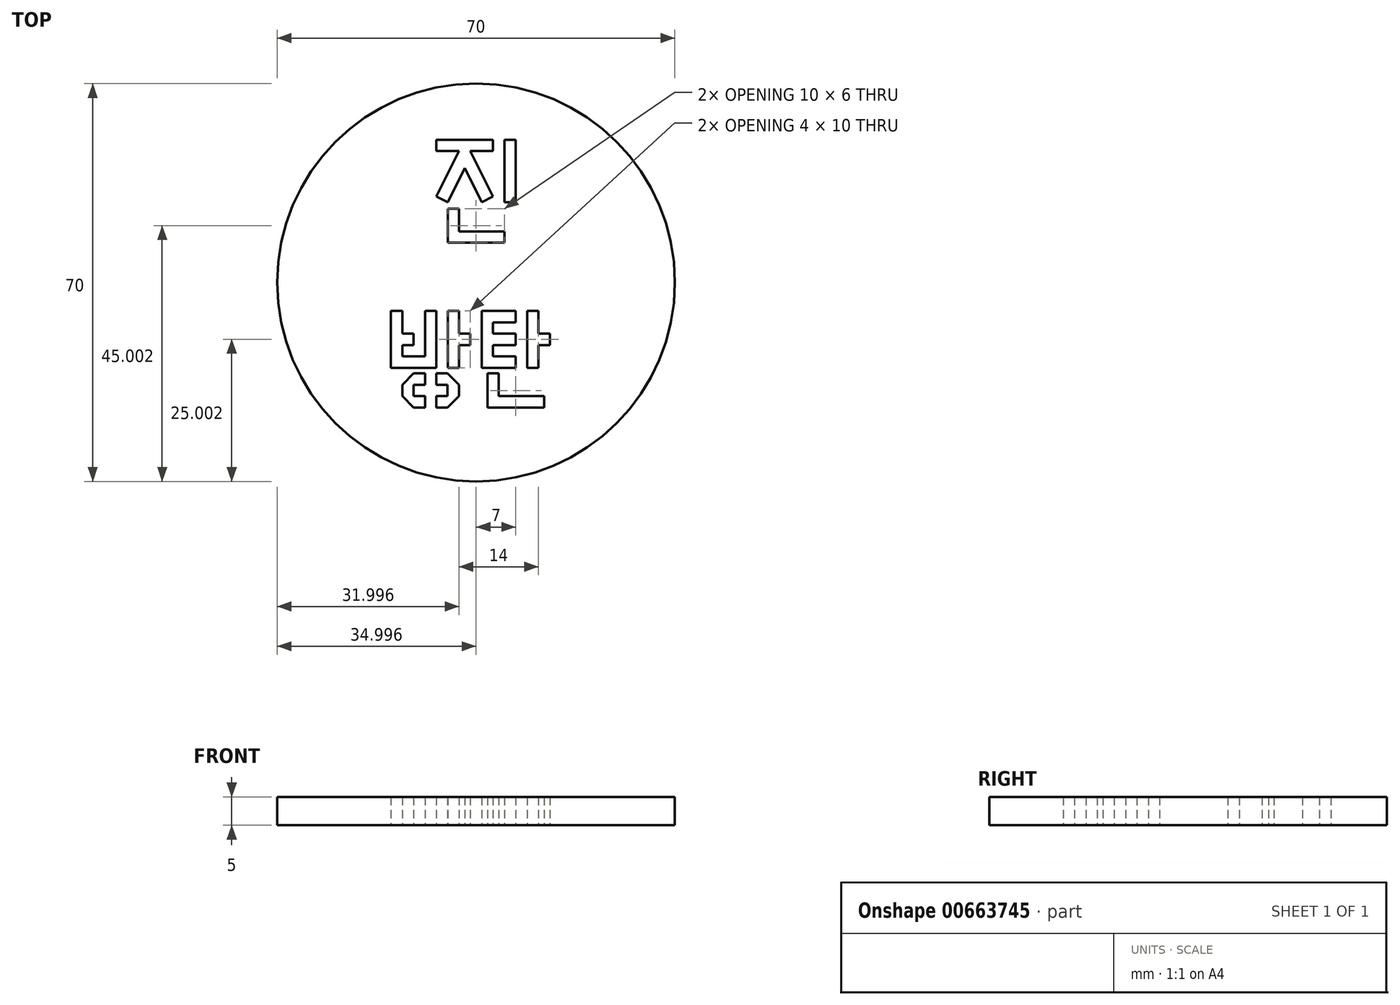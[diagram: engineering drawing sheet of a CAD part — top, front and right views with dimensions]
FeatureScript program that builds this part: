
annotation { "Feature Type Name" : "Feature", "Feature Type Description" : "" }
export const myFeature = defineFeature(function(context is Context, id is Id, definition is map)
    precondition{}
    {
        {
            var Q0;
            Q0=qCreatedBy(makeId("Top.planeOp"),FACE);
            var sketch = newSketch(context, id + "F0", { "sketchPlane" : qUnion([Q0])});
            skLineSegment(sketch, "E0.bottom", {"start": v(-33.94, 20.88) * mm, "end": v(-23.94, 20.88) * mm});
            skLineSegment(sketch, "E0.left", {"start": v(-33.94, 20.88) * mm, "end": v(-33.94, 18.88) * mm});
            skLineSegment(sketch, "E0.right", {"start": v(-23.94, 20.88) * mm, "end": v(-23.94, 18.88) * mm});
            skLineSegment(sketch, "E1", {"start": v(-33.94, 18.88) * mm, "end": v(-29.94, 18.88) * mm});
            skLineSegment(sketch, "E2", {"start": v(-29.94, 18.88) * mm, "end": v(-33.94, 10.88) * mm});
            skLineSegment(sketch, "E3", {"start": v(-33.94, 10.88) * mm, "end": v(-31.94, 9.88) * mm});
            skLineSegment(sketch, "E4", {"start": v(-31.94, 9.88) * mm, "end": v(-28.94, 15.88) * mm});
            skLineSegment(sketch, "E5", {"start": v(-28.94, 15.88) * mm, "end": v(-25.94, 9.88) * mm});
            skLineSegment(sketch, "E6", {"start": v(-25.94, 9.88) * mm, "end": v(-23.94, 10.88) * mm});
            skLineSegment(sketch, "E7", {"start": v(-27.94, 18.88) * mm, "end": v(-23.94, 10.88) * mm});
            skLineSegment(sketch, "E8.bottom", {"start": v(-21.94, 9.88) * mm, "end": v(-19.94, 9.88) * mm});
            skLineSegment(sketch, "E8.left", {"start": v(-21.94, 9.88) * mm, "end": v(-21.94, 20.88) * mm});
            skLineSegment(sketch, "E9", {"start": v(-29.94, 5.75) * mm, "end": v(-29.94, 8.75) * mm});
            skLineSegment(sketch, "E10.bottom", {"start": v(-25.94, -9.25) * mm, "end": v(-19.94, -9.25) * mm});
            skLineSegment(sketch, "E10.top", {"start": v(-25.94, -19.25) * mm, "end": v(-19.94, -19.25) * mm});
            skLineSegment(sketch, "E10.left", {"start": v(-25.94, -9.25) * mm, "end": v(-25.94, -19.25) * mm});
            skLineSegment(sketch, "E10.right", {"start": v(-19.94, -9.25) * mm, "end": v(-19.94, -11.25) * mm});
            skLineSegment(sketch, "E11", {"start": v(-19.94, -11.25) * mm, "end": v(-23.94, -11.25) * mm});
            skLineSegment(sketch, "E12", {"start": v(-23.94, -11.25) * mm, "end": v(-23.94, -13.25) * mm});
            skLineSegment(sketch, "E13", {"start": v(-23.94, -13.25) * mm, "end": v(-19.94, -13.25) * mm});
            skLineSegment(sketch, "E14", {"start": v(-19.94, -13.25) * mm, "end": v(-19.94, -15.25) * mm});
            skLineSegment(sketch, "E15", {"start": v(-19.94, -15.25) * mm, "end": v(-23.94, -15.25) * mm});
            skLineSegment(sketch, "E16", {"start": v(-23.94, -15.25) * mm, "end": v(-23.94, -17.25) * mm});
            skLineSegment(sketch, "E17", {"start": v(-23.94, -17.25) * mm, "end": v(-19.94, -17.25) * mm});
            skLineSegment(sketch, "E18.bottom", {"start": v(-17.94, -9.25) * mm, "end": v(-15.94, -9.25) * mm});
            skLineSegment(sketch, "E18.top", {"start": v(-17.94, -19.25) * mm, "end": v(-15.94, -19.25) * mm});
            skLineSegment(sketch, "E18.left", {"start": v(-17.94, -9.25) * mm, "end": v(-17.94, -19.25) * mm});
            skLineSegment(sketch, "E18.right", {"start": v(-15.94, -9.25) * mm, "end": v(-15.94, -13.25) * mm});
            skLineSegment(sketch, "E19.bottom", {"start": v(-15.94, -13.25) * mm, "end": v(-13.94, -13.25) * mm});
            skLineSegment(sketch, "E19.top", {"start": v(-15.94, -15.25) * mm, "end": v(-13.94, -15.25) * mm});
            skLineSegment(sketch, "E19.right", {"start": v(-13.94, -13.25) * mm, "end": v(-13.94, -15.25) * mm});
            skLineSegment(sketch, "E20", {"start": v(-25.94, -19.25) * mm, "end": v(-24.94, -19.25) * mm});
            skLineSegment(sketch, "E21", {"start": v(-24.94, -20.25) * mm, "end": v(-24.94, -26.25) * mm});
            skLineSegment(sketch, "E22", {"start": v(-24.94, -26.25) * mm, "end": v(-14.94, -26.25) * mm});
            skLineSegment(sketch, "E23", {"start": v(-14.94, -26.25) * mm, "end": v(-14.94, -24.25) * mm});
            skLineSegment(sketch, "E24", {"start": v(-14.94, -24.25) * mm, "end": v(-22.94, -24.25) * mm});
            skLineSegment(sketch, "E25", {"start": v(-22.94, -24.25) * mm, "end": v(-22.94, -20.25) * mm});
            skLineSegment(sketch, "E26", {"start": v(-22.94, -20.25) * mm, "end": v(-24.94, -20.25) * mm});
            skLineSegment(sketch, "E27", {"start": v(-29.94, -9.25) * mm, "end": v(-31.94, -9.25) * mm});
            skLineSegment(sketch, "E28", {"start": v(-41.94, -9.25) * mm, "end": v(-41.94, -19.25) * mm});
            skLineSegment(sketch, "E29", {"start": v(-41.94, -19.25) * mm, "end": v(-33.94, -19.25) * mm});
            skLineSegment(sketch, "E30", {"start": v(-33.94, -19.25) * mm, "end": v(-33.94, -9.25) * mm});
            skLineSegment(sketch, "E31.bottom", {"start": v(-31.94, -9.25) * mm, "end": v(-29.94, -9.25) * mm});
            skLineSegment(sketch, "E31.top", {"start": v(-31.94, -19.25) * mm, "end": v(-29.94, -19.25) * mm});
            skLineSegment(sketch, "E31.left", {"start": v(-31.94, -9.25) * mm, "end": v(-31.94, -19.25) * mm});
            skLineSegment(sketch, "E31.right", {"start": v(-29.94, -9.25) * mm, "end": v(-29.94, -13.25) * mm});
            skLineSegment(sketch, "E32", {"start": v(-29.94, -19.25) * mm, "end": v(-29.94, -15.25) * mm});
            skLineSegment(sketch, "E33.bottom", {"start": v(-29.94, -15.25) * mm, "end": v(-27.94, -15.25) * mm});
            skLineSegment(sketch, "E33.top", {"start": v(-29.94, -13.25) * mm, "end": v(-27.94, -13.25) * mm});
            skLineSegment(sketch, "E33.right", {"start": v(-27.94, -15.25) * mm, "end": v(-27.94, -13.25) * mm});
            skLineSegment(sketch, "E34", {"start": v(-41.94, -9.25) * mm, "end": v(-39.94, -9.25) * mm});
            skLineSegment(sketch, "E35", {"start": v(-39.94, -9.25) * mm, "end": v(-39.94, -13.25) * mm});
            skLineSegment(sketch, "E36", {"start": v(-39.94, -13.25) * mm, "end": v(-37.94, -13.25) * mm});
            skLineSegment(sketch, "E37", {"start": v(-37.94, -13.25) * mm, "end": v(-37.94, -15.25) * mm});
            skLineSegment(sketch, "E38", {"start": v(-37.94, -15.25) * mm, "end": v(-39.94, -15.25) * mm});
            skLineSegment(sketch, "E39", {"start": v(-39.94, -15.25) * mm, "end": v(-39.94, -17.25) * mm});
            skLineSegment(sketch, "E40", {"start": v(-39.94, -17.25) * mm, "end": v(-35.94, -17.25) * mm});
            skLineSegment(sketch, "E41", {"start": v(-35.94, -17.25) * mm, "end": v(-35.94, -9.25) * mm});
            skLineSegment(sketch, "E42", {"start": v(-41.94, -19.25) * mm, "end": v(-39.94, -19.25) * mm});
            skLineSegment(sketch, "E43.bottom", {"start": v(-37.94, -20.25) * mm, "end": v(-35.94, -20.25) * mm});
            skLineSegment(sketch, "E43.top", {"start": v(-37.94, -26.25) * mm, "end": v(-35.94, -26.25) * mm});
            skLineSegment(sketch, "E43.left", {"start": v(-39.94, -22.25) * mm, "end": v(-39.94, -24.25) * mm});
            skLineSegment(sketch, "E44", {"start": v(-37.94, -20.25) * mm, "end": v(-39.94, -22.25) * mm});
            skLineSegment(sketch, "E45", {"start": v(-39.94, -24.25) * mm, "end": v(-37.94, -26.25) * mm});
            skLineSegment(sketch, "E46", {"start": v(-35.94, -20.25) * mm, "end": v(-35.94, -22.25) * mm});
            skLineSegment(sketch, "E47", {"start": v(-35.94, -22.25) * mm, "end": v(-37.94, -22.25) * mm});
            skLineSegment(sketch, "E48", {"start": v(-37.94, -22.25) * mm, "end": v(-37.94, -24.25) * mm});
            skLineSegment(sketch, "E49", {"start": v(-37.94, -24.25) * mm, "end": v(-35.94, -24.25) * mm});
            skLineSegment(sketch, "E50", {"start": v(-35.94, -24.25) * mm, "end": v(-35.94, -26.25) * mm});
            skLineSegment(sketch, "E51.MirrorCS", {"start": v(-29.95, -22.25) * mm, "end": v(-29.95, -24.25) * mm});
            skLineSegment(sketch, "E52.MirrorCS", {"start": v(-33.94, -24.25) * mm, "end": v(-33.94, -26.25) * mm});
            skLineSegment(sketch, "E53.MirrorCS", {"start": v(-31.94, -24.25) * mm, "end": v(-33.94, -24.25) * mm});
            skLineSegment(sketch, "E54.MirrorCS", {"start": v(-31.94, -22.25) * mm, "end": v(-31.94, -24.25) * mm});
            skLineSegment(sketch, "E55.MirrorCS", {"start": v(-29.95, -24.25) * mm, "end": v(-31.94, -26.25) * mm});
            skLineSegment(sketch, "E56.MirrorCS", {"start": v(-33.94, -22.25) * mm, "end": v(-31.94, -22.25) * mm});
            skLineSegment(sketch, "E57.MirrorCS", {"start": v(-31.94, -26.25) * mm, "end": v(-33.94, -26.25) * mm});
            skLineSegment(sketch, "E58.MirrorCS", {"start": v(-31.94, -20.25) * mm, "end": v(-33.94, -20.25) * mm});
            skLineSegment(sketch, "E59.MirrorCS", {"start": v(-33.94, -20.25) * mm, "end": v(-33.94, -22.25) * mm});
            skLineSegment(sketch, "E60.MirrorCS", {"start": v(-31.94, -20.25) * mm, "end": v(-29.95, -22.25) * mm});
            skLineSegment(sketch, "E61.trimOffspring", {"start": v(-39.94, -9.25) * mm, "end": v(-41.94, -9.25) * mm});
            skLineSegment(sketch, "E62.trimOffspring", {"start": v(-33.94, -9.25) * mm, "end": v(-35.94, -9.25) * mm});
            skLineSegment(sketch, "E63.trimOffspring", {"start": v(-15.94, -15.25) * mm, "end": v(-15.94, -19.25) * mm});
            skLineSegment(sketch, "E64.trimOffspring", {"start": v(-19.94, -17.25) * mm, "end": v(-19.94, -19.25) * mm});
            skLineSegment(sketch, "E65.trimOffspring", {"start": v(-29.94, -15.25) * mm, "end": v(-29.94, -19.25) * mm});
            skCircle(sketch, "E66", {"center": v(-26.94, -4.25) * mm, "radius": 35 * mm});
            skLineSegment(sketch, "E67.trimOffspring", {"start": v(-27.94, 18.88) * mm, "end": v(-23.94, 18.88) * mm});
            skLineSegment(sketch, "E68", {"start": v(-31.94, 8.75) * mm, "end": v(-29.94, 8.75) * mm});
            skLineSegment(sketch, "E69", {"start": v(-29.94, 5.75) * mm, "end": v(-29.94, 4.75) * mm});
            skLineSegment(sketch, "E70", {"start": v(-29.94, 4.75) * mm, "end": v(-21.94, 4.75) * mm});
            skLineSegment(sketch, "E71", {"start": v(-31.94, 8.75) * mm, "end": v(-31.94, 2.75) * mm});
            skLineSegment(sketch, "E72", {"start": v(-31.94, 2.75) * mm, "end": v(-21.94, 2.75) * mm});
            skLineSegment(sketch, "E73", {"start": v(-21.94, 2.75) * mm, "end": v(-21.94, 4.75) * mm});
            skLineSegment(sketch, "E74", {"start": v(-21.94, 20.88) * mm, "end": v(-19.94, 20.88) * mm});
            skLineSegment(sketch, "E75", {"start": v(-19.94, 20.88) * mm, "end": v(-19.94, 9.88) * mm});
            skSolve(sketch);
        }
        {
            var Q0;
            Q0=makeQuery(id+"F0.imprint","IMPRINT",FACE,{"disambiguationData":[TD([[makeQuery(id+"F0.imprint","IMPRINT",EDGE,{"derivedFrom":sQuery(id+"F0.wireOp",EDGE,"E0.bottom")}),1.0]])]});
            extrude(context, id + "F1", {"entities" : qUnion([Q0]), "depth" : 5 * mm, "offsetDistance" : 25 * mm});
        }
    });
